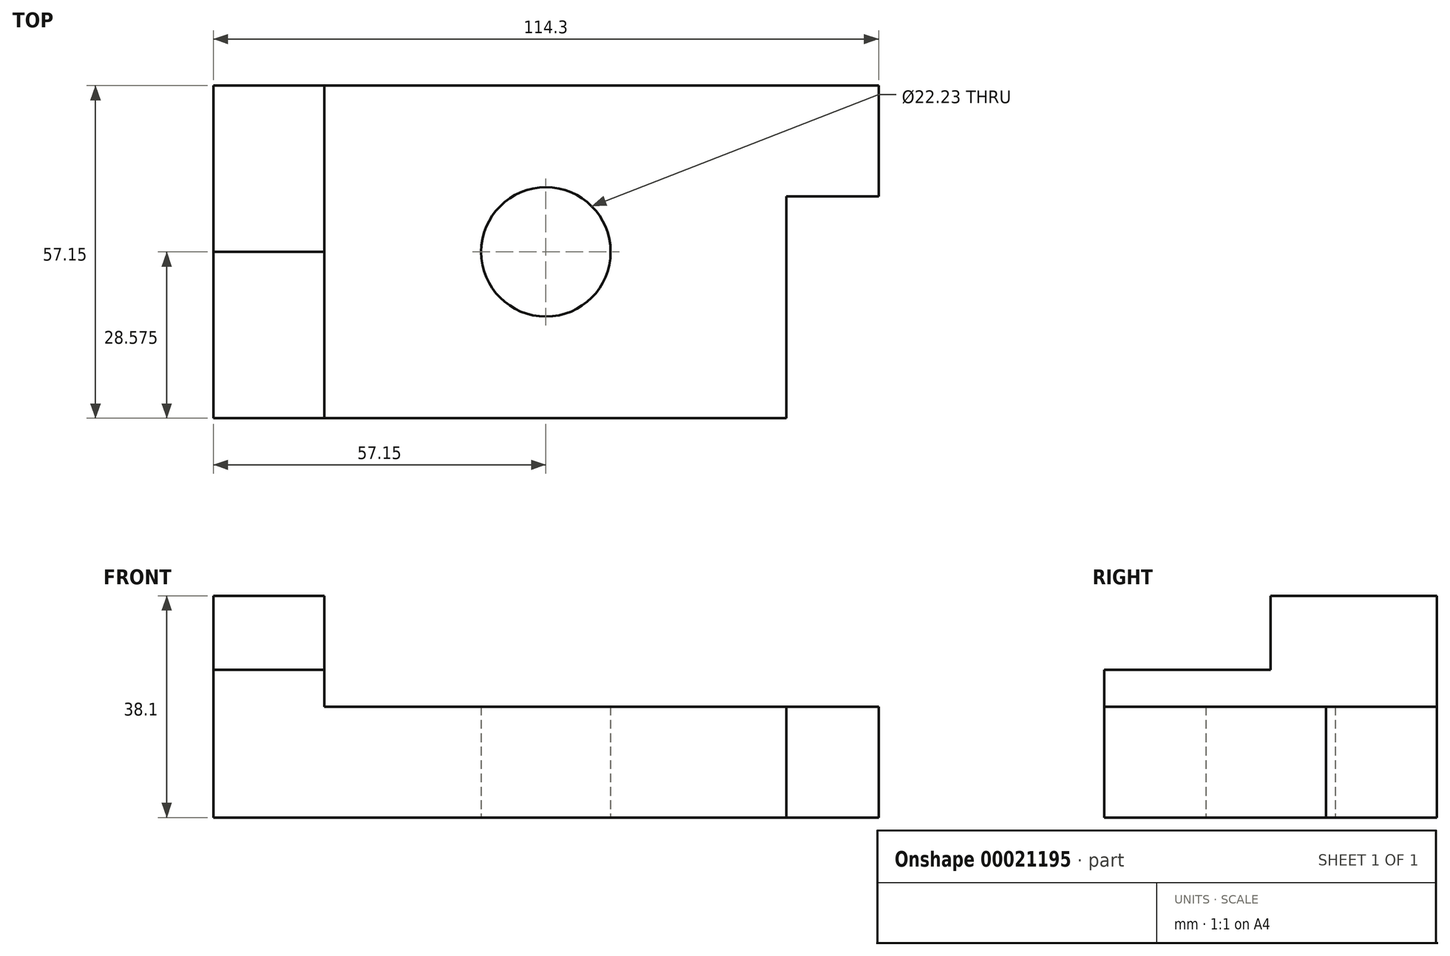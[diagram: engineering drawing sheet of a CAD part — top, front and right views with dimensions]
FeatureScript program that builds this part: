
annotation { "Feature Type Name" : "Feature", "Feature Type Description" : "" }
export const myFeature = defineFeature(function(context is Context, id is Id, definition is map)
    precondition{}
    {
        {
            var Q0;
            Q0=qCreatedBy(makeId("Top.planeOp"),FACE);
            var sketch = newSketch(context, id + "F0", { "sketchPlane" : qUnion([Q0])});
            skLineSegment(sketch, "E0.bottom", {"start": v(0, 0) * mm, "end": v(114.3, 0) * mm});
            skLineSegment(sketch, "E0.top", {"start": v(0, -57.15) * mm, "end": v(98.43, -57.15) * mm});
            skLineSegment(sketch, "E0.left", {"start": v(0, 0) * mm, "end": v(0, -57.15) * mm});
            skLineSegment(sketch, "E0.right", {"start": v(114.3, 0) * mm, "end": v(114.3, -19.05) * mm});
            skLineSegment(sketch, "E1.top", {"start": v(114.3, -19.05) * mm, "end": v(98.43, -19.05) * mm});
            skLineSegment(sketch, "E1.right", {"start": v(98.43, -57.15) * mm, "end": v(98.43, -19.05) * mm});
            skCircle(sketch, "E2", {"center": v(57.15, -28.58) * mm, "radius": 11.11 * mm});
            skPoint(sketch, "E3.orphan", {"position": v(57.15, 0) * mm});
            skPoint(sketch, "E4.start.orphan", {"position": v(114.3, -28.58) * mm});
            skSolve(sketch);
        }
        {
            var Q0;
            Q0 = qSketchRegion(id + "F0", true);
            extrude(context, id + "F1", {"entities" : qUnion([Q0]), "depth" : 19.05 * mm});
        }
        {
            var Q0;
            Q0=makeQuery(id+"F1.opExtrude","CAP_FACE",FACE,{"disambiguationData":[OSD([sQuery(id+"F0.wireOp",EDGE,"E0.bottom"),sQuery(id+"F0.wireOp",EDGE,"E0.top"),sQuery(id+"F0.wireOp",EDGE,"E0.left"),sQuery(id+"F0.wireOp",EDGE,"E0.right"),sQuery(id+"F0.wireOp",EDGE,"E1.top"),sQuery(id+"F0.wireOp",EDGE,"E1.right"),sQuery(id+"F0.wireOp",EDGE,"E2")])],"isStart":false});
            var sketch = newSketch(context, id + "F2", { "sketchPlane" : qUnion([Q0])});
            skLineSegment(sketch, "E5.bottom", {"start": v(0, -57.15) * mm, "end": v(19.05, -57.15) * mm});
            skLineSegment(sketch, "E5.top", {"start": v(0, 0) * mm, "end": v(19.05, 0) * mm});
            skLineSegment(sketch, "E5.left", {"start": v(0, -57.15) * mm, "end": v(0, 0) * mm});
            skLineSegment(sketch, "E5.right", {"start": v(19.05, -57.15) * mm, "end": v(19.05, 0) * mm});
            skSolve(sketch);
        }
        {
            var Q0;
            Q0 = qSketchRegion(id + "F2", true);
            extrude(context, id + "F3", {"entities" : qUnion([Q0]), "operationType" : NewBodyOperationType.ADD, "depth" : 6.35 * mm});
        }
        {
            var Q0;
            Q0=makeQuery(id+"F3.opExtrude","CAP_FACE",FACE,{"disambiguationData":[OSD([sQuery(id+"F2.wireOp",EDGE,"E5.bottom"),sQuery(id+"F2.wireOp",EDGE,"E5.top"),sQuery(id+"F2.wireOp",EDGE,"E5.left"),sQuery(id+"F2.wireOp",EDGE,"E5.right")])],"isStart":false});
            var sketch = newSketch(context, id + "F4", { "sketchPlane" : qUnion([Q0])});
            skLineSegment(sketch, "E6.bottom", {"start": v(0, 0) * mm, "end": v(19.05, 0) * mm});
            skLineSegment(sketch, "E6.top", {"start": v(0, -28.57) * mm, "end": v(19.05, -28.57) * mm});
            skLineSegment(sketch, "E6.left", {"start": v(0, 0) * mm, "end": v(0, -28.57) * mm});
            skLineSegment(sketch, "E6.right", {"start": v(19.05, 0) * mm, "end": v(19.05, -28.57) * mm});
            skSolve(sketch);
        }
        {
            var Q0;
            Q0 = qSketchRegion(id + "F4", true);
            extrude(context, id + "F5", {"entities" : qUnion([Q0]), "operationType" : NewBodyOperationType.ADD, "depth" : 12.7 * mm});
        }
    });
